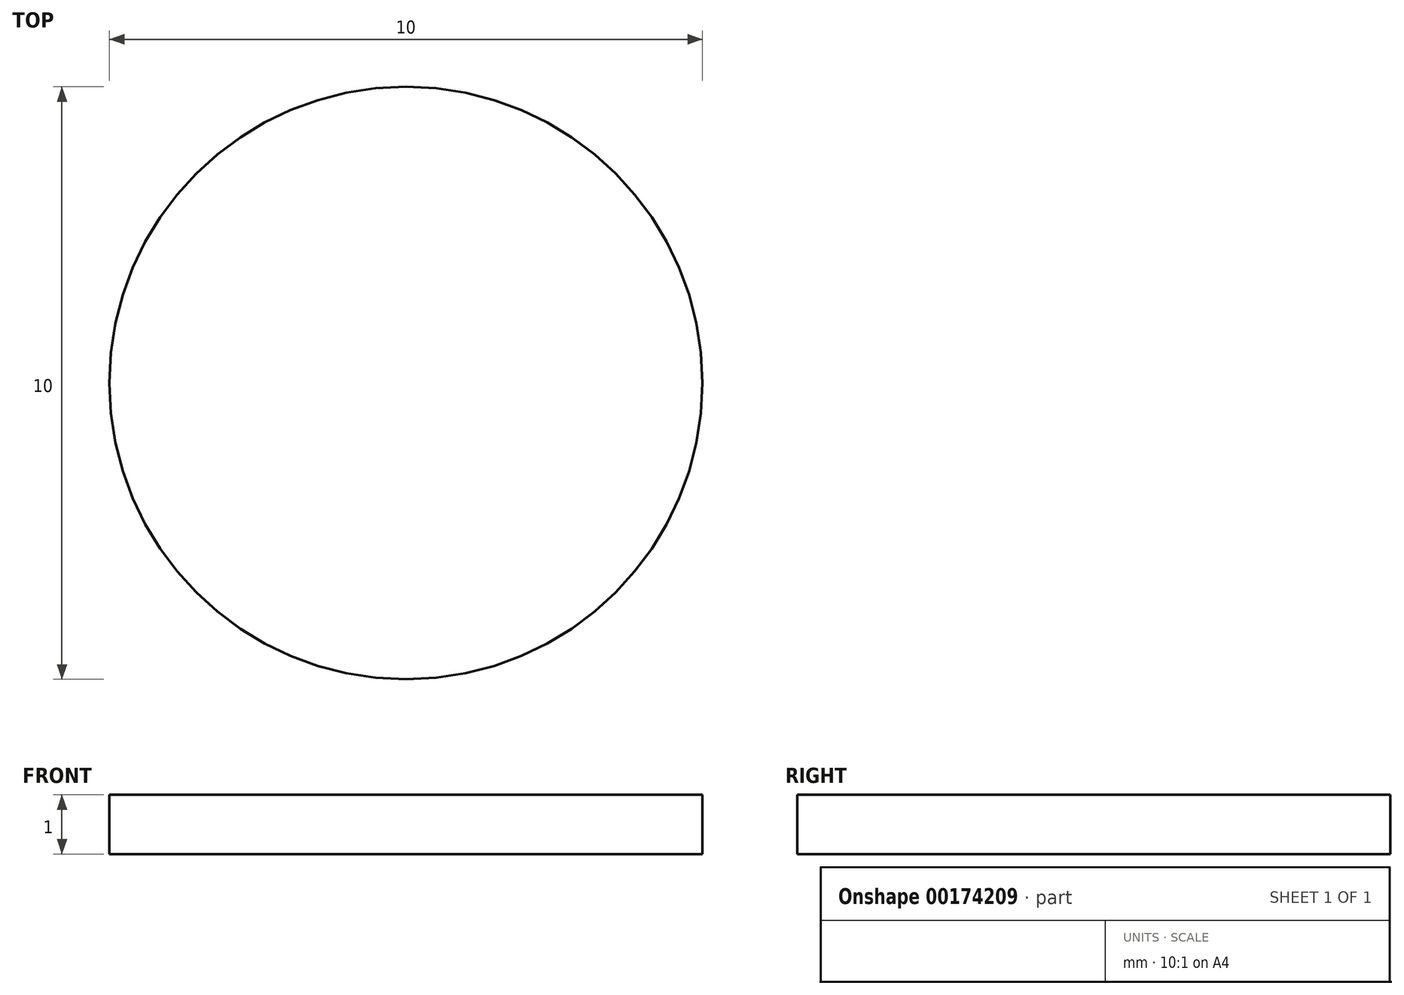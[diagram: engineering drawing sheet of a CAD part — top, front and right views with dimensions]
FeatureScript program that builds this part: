
annotation { "Feature Type Name" : "Feature", "Feature Type Description" : "" }
export const myFeature = defineFeature(function(context is Context, id is Id, definition is map)
    precondition{}
    {
        {
            var Q0;
            Q0=qCreatedBy(makeId("Top.planeOp"),FACE);
            var sketch = newSketch(context, id + "F0", { "sketchPlane" : qUnion([Q0])});
            skCircle(sketch, "E0", {"center": v(0, 0) * mm, "radius": 5 * mm});
            skSolve(sketch);
        }
        {
            var Q0;
            Q0=makeQuery(id+"F0.imprint","IMPRINT",FACE,{"disambiguationData":[TD([[makeQuery(id+"F0.imprint","IMPRINT",EDGE,{"derivedFrom":sQuery(id+"F0.wireOp",EDGE,"E0")}),1.0]])]});
            extrude(context, id + "F1", {"entities" : qUnion([Q0]), "depth" : 1 * mm});
        }
    });
